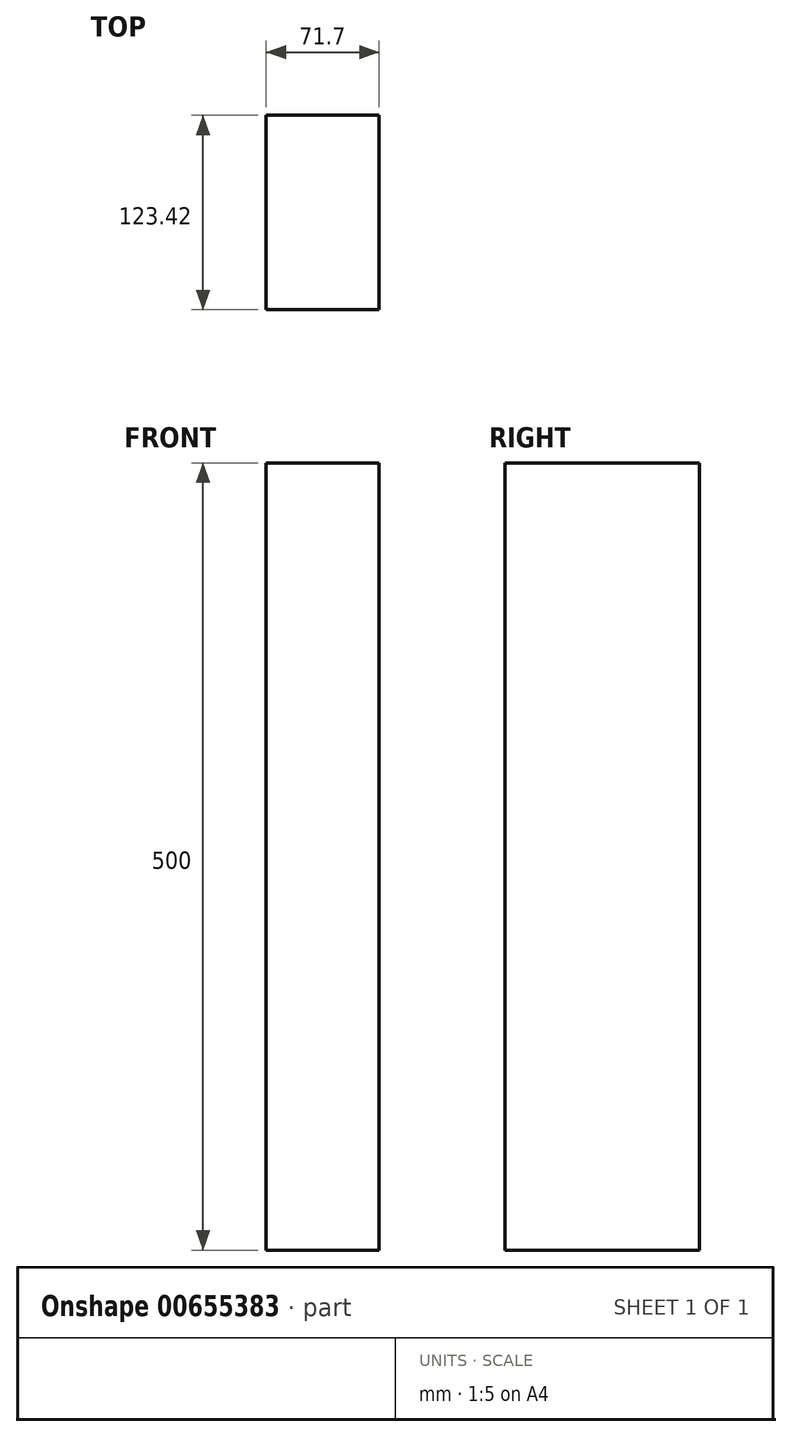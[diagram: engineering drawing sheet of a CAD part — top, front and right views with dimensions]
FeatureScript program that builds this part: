
annotation { "Feature Type Name" : "Feature", "Feature Type Description" : "" }
export const myFeature = defineFeature(function(context is Context, id is Id, definition is map)
    precondition{}
    {
        {
            var Q0;
            Q0=qCreatedBy(makeId("Top.planeOp"),FACE);
            var sketch = newSketch(context, id + "F0", { "sketchPlane" : qUnion([Q0])});
            skLineSegment(sketch, "E0.bottom", {"start": v(35.85, 61.71) * mm, "end": v(-35.85, 61.71) * mm});
            skLineSegment(sketch, "E0.top", {"start": v(35.85, -61.71) * mm, "end": v(-35.85, -61.71) * mm});
            skLineSegment(sketch, "E0.left", {"start": v(35.85, 61.71) * mm, "end": v(35.85, -61.71) * mm});
            skLineSegment(sketch, "E0.right", {"start": v(-35.85, 61.71) * mm, "end": v(-35.85, -61.71) * mm});
            skPoint(sketch, "E0.middle", {"position": v(0, 0) * mm});
            skSolve(sketch);
        }
        {
            var Q0;
            Q0 = qSketchRegion(id + "F0", true);
            extrude(context, id + "F1", {"entities" : qUnion([Q0]), "depth" : 500 * mm, "offsetDistance" : 25.4 * mm});
        }
    });
